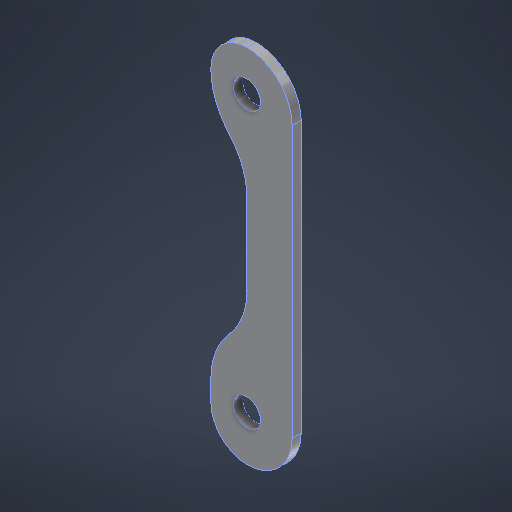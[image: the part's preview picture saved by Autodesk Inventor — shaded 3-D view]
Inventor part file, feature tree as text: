
AUTODESK INVENTOR PART (.ipt)
format: ipt  version: 2025.3 (Build 293356000, 356)  size: 235,008 bytes
history: native  units: in
note: dims shown in document units (in); Inventor stores cm internally (conversion verified against a paired STEP export)
features: fillet x4, extrude x1, sketch x1
ambient origin geometry x8: Origin, YZ Plane, XZ Plane, XY Plane, X Axis, Y Axis, Z Axis, Center Point
bodies: Solid1 (feature_tree)
feature tree (6):
  extrude  "Extrusion1"  Depth=0.3071in
  fillet  "Fillet9"  Radius=0.0394in
  fillet  "Fillet10"  Radius=0.1575in
  fillet  "Fillet11"  Radius=0.3543in
  fillet  "Fillet12"  Radius=0.3543in
  sketch  "Sketch1"  dims[d0=0.1181in d1=0.1181in d10=0.0394in d11=0.0in d13=0.1575in d14=0.1969in d47=0.3543in d48=0.3543in d49=0.1969in d50=0.1575in d51=0.3071in d52=0.1575in d55=0.1772in d59=1.5748in d60=0.0984in d61=0.0984in d62=0.3071in]
